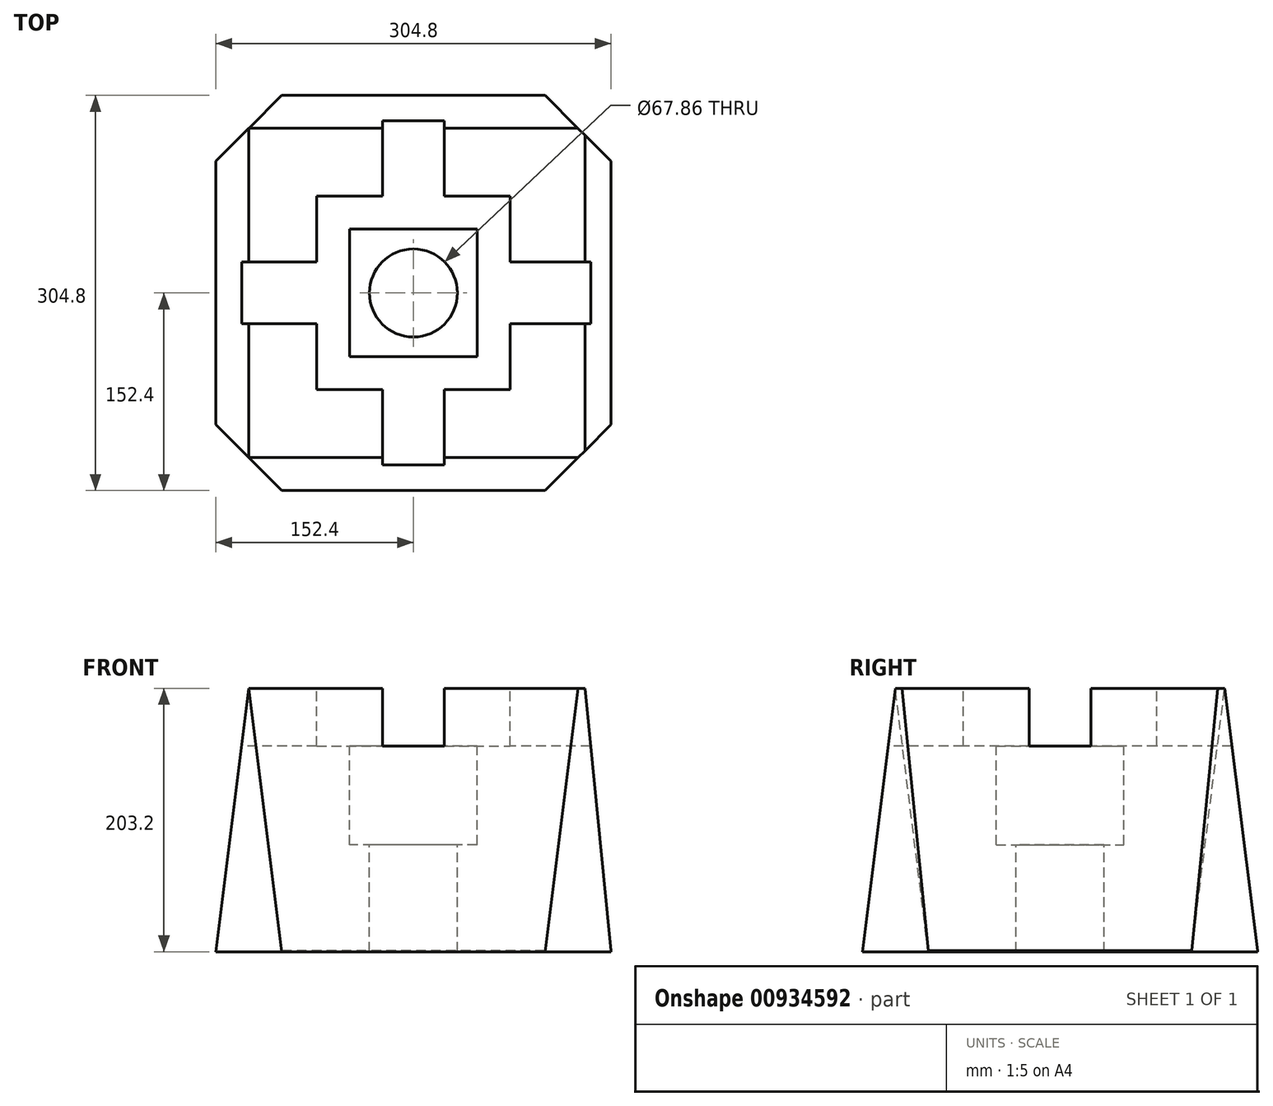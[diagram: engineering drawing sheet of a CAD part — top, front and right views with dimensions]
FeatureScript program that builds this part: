
annotation { "Feature Type Name" : "Feature", "Feature Type Description" : "" }
export const myFeature = defineFeature(function(context is Context, id is Id, definition is map)
    precondition{}
    {
        {
            var Q0;
            Q0=qCreatedBy(makeId("Top.planeOp"),FACE);
            var sketch = newSketch(context, id + "F0", { "sketchPlane" : qUnion([Q0])});
            skLineSegment(sketch, "E0.bottom", {"start": v(0, 0) * mm, "end": v(304.8, 0) * mm});
            skLineSegment(sketch, "E0.top", {"start": v(0, 304.8) * mm, "end": v(304.8, 304.8) * mm});
            skLineSegment(sketch, "E0.left", {"start": v(0, 0) * mm, "end": v(0, 304.8) * mm});
            skLineSegment(sketch, "E0.right", {"start": v(304.8, 0) * mm, "end": v(304.8, 304.8) * mm});
            skSolve(sketch);
        }
        {
            var Q0;
            Q0=makeQuery(id+"F0.imprint","IMPRINT",FACE,{"disambiguationData":[TD([[makeQuery(id+"F0.imprint","IMPRINT",EDGE,{"derivedFrom":sQuery(id+"F0.wireOp",EDGE,"E0.bottom")}),1.0]])]});
            extrude(context, id + "F1", {"entities" : qUnion([Q0]), "depth" : 203.2 * mm, "offsetDistance" : 25.4 * mm});
        }
        {
            var Q0;
            Q0=makeQuery(id+"F1.opExtrude","CAP_FACE",FACE,{"disambiguationData":[OSD([sQuery(id+"F0.wireOp",EDGE,"E0.bottom"),sQuery(id+"F0.wireOp",EDGE,"E0.top"),sQuery(id+"F0.wireOp",EDGE,"E0.left"),sQuery(id+"F0.wireOp",EDGE,"E0.right")])],"isStart":false});
            var sketch = newSketch(context, id + "F2", { "sketchPlane" : qUnion([Q0])});
            skLineSegment(sketch, "E1.bottom", {"start": v(77.79, 227.01) * mm, "end": v(227.01, 227.01) * mm});
            skLineSegment(sketch, "E1.top", {"start": v(77.79, 77.79) * mm, "end": v(227.01, 77.79) * mm});
            skLineSegment(sketch, "E1.left", {"start": v(77.79, 227.01) * mm, "end": v(77.79, 77.79) * mm});
            skLineSegment(sketch, "E1.right", {"start": v(227.01, 227.01) * mm, "end": v(227.01, 77.79) * mm});
            skSolve(sketch);
        }
        {
            var Q0;
            Q0=makeQuery(id+"F2.imprint","IMPRINT",FACE,{"disambiguationData":[TD([[makeQuery(id+"F2.imprint","IMPRINT",EDGE,{"derivedFrom":sQuery(id+"F2.wireOp",EDGE,"E1.bottom")}),-1.0]])]});
            extrude(context, id + "F3", {"entities" : qUnion([Q0]), "operationType" : NewBodyOperationType.REMOVE, "oppositeDirection" : true, "depth" : 44.45 * mm, "offsetDistance" : 25.4 * mm});
        }
        {
            var Q0;
            Q0=makeQuery(id+"F1.opExtrude","CAP_FACE",FACE,{"disambiguationData":[OSD([sQuery(id+"F0.wireOp",EDGE,"E0.bottom"),sQuery(id+"F0.wireOp",EDGE,"E0.top"),sQuery(id+"F0.wireOp",EDGE,"E0.left"),sQuery(id+"F0.wireOp",EDGE,"E0.right")])],"isStart":false});
            var sketch = newSketch(context, id + "F4", { "sketchPlane" : qUnion([Q0])});
            skLineSegment(sketch, "E2.bottom", {"start": v(128.59, 304.8) * mm, "end": v(176.21, 304.8) * mm});
            skLineSegment(sketch, "E2.top", {"start": v(128.59, 0) * mm, "end": v(176.21, 0) * mm});
            skLineSegment(sketch, "E2.left", {"start": v(128.59, 304.8) * mm, "end": v(128.59, 0) * mm});
            skLineSegment(sketch, "E2.right", {"start": v(176.21, 304.8) * mm, "end": v(176.21, 0) * mm});
            skLineSegment(sketch, "E3.bottom", {"start": v(312.2, 128.59) * mm, "end": v(-17, 128.59) * mm});
            skLineSegment(sketch, "E3.top", {"start": v(312.2, 176.21) * mm, "end": v(-17, 176.21) * mm});
            skLineSegment(sketch, "E3.left", {"start": v(312.2, 128.59) * mm, "end": v(312.2, 176.21) * mm});
            skLineSegment(sketch, "E3.right", {"start": v(-17, 128.59) * mm, "end": v(-17, 176.21) * mm});
            skSolve(sketch);
        }
        {
            var Q0;
            {var subQ0=sQuery(id+"F4.wireOp",EDGE,"E2.bottom");Q0=makeQuery(id+"F4.imprint","IMPRINT",FACE,{"disambiguationData":[TD([[makeQuery(id+"F4.imprint","IMPRINT",EDGE,{"derivedFrom":subQ0}),-1.0]])]});}
            var Q1;
            {var subQ0=sQuery(id+"F4.wireOp",EDGE,"E2.top");Q1=makeQuery(id+"F4.imprint","IMPRINT",FACE,{"disambiguationData":[TD([[makeQuery(id+"F4.imprint","IMPRINT",EDGE,{"derivedFrom":subQ0}),1.0]])]});}
            var Q2;
            {var subQ0=sQuery(id+"F4.wireOp",EDGE,"E3.bottom");var subQ1=makeQuery(id+"F1.opExtrude","CAP_EDGE",EDGE,{"disambiguationData":[OSD([sQuery(id+"F0.wireOp",EDGE,"E0.right")])],"isStart":false});var subQ2=makeQuery(id+"F4.imprint","INTERSECT",VERTEX,{"derivedFrom":[subQ1,subQ0]});Q2=makeQuery(id+"F4.imprint","IMPRINT",FACE,{"disambiguationData":[TD([[makeQuery(id+"F4.imprint","IMPRINT",EDGE,{"disambiguationData":[TD([[subQ2,-1.0]])],"derivedFrom":subQ0}),-1.0]])]});}
            var Q3;
            {var subQ0=sQuery(id+"F4.wireOp",EDGE,"E3.bottom");var subQ1=makeQuery(id+"F1.opExtrude","CAP_EDGE",EDGE,{"disambiguationData":[OSD([sQuery(id+"F0.wireOp",EDGE,"E0.left")])],"isStart":false});var subQ2=makeQuery(id+"F4.imprint","INTERSECT",VERTEX,{"derivedFrom":[subQ1,subQ0]});Q3=makeQuery(id+"F4.imprint","IMPRINT",FACE,{"disambiguationData":[TD([[makeQuery(id+"F4.imprint","IMPRINT",EDGE,{"disambiguationData":[TD([[subQ2,1.0]])],"derivedFrom":subQ0}),-1.0]])]});}
            extrude(context, id + "F5", {"entities" : qUnion([Q0, Q1, Q2, Q3]), "operationType" : NewBodyOperationType.REMOVE, "oppositeDirection" : true, "depth" : 44.45 * mm, "offsetDistance" : 25.4 * mm});
        }
        {
            var Q0;
            Q0=makeQuery(id+"F1.opExtrude","SWEPT_EDGE",EDGE,{"disambiguationData":[OSD([sQuery(id+"F0.wireOp",EDGE,"E0.bottom"),sQuery(id+"F0.wireOp",EDGE,"E0.right")])]});
            var Q1;
            Q1=makeQuery(id+"F1.opExtrude","SWEPT_EDGE",EDGE,{"disambiguationData":[OSD([sQuery(id+"F0.wireOp",EDGE,"E0.top"),sQuery(id+"F0.wireOp",EDGE,"E0.right")])]});
            var Q2;
            Q2=makeQuery(id+"F1.opExtrude","SWEPT_EDGE",EDGE,{"disambiguationData":[OSD([sQuery(id+"F0.wireOp",EDGE,"E0.bottom"),sQuery(id+"F0.wireOp",EDGE,"E0.left")])]});
            var Q3;
            Q3=makeQuery(id+"F1.opExtrude","SWEPT_EDGE",EDGE,{"disambiguationData":[OSD([sQuery(id+"F0.wireOp",EDGE,"E0.top"),sQuery(id+"F0.wireOp",EDGE,"E0.left")])]});
            chamfer(context, id + "F6", {"entities" : qUnion([Q0, Q1, Q2, Q3]), "width" : 50.8 * mm, "tangentPropagation" : true});
        }
        {
            var Q0;
            Q0=makeQuery(id+"F3.boolean.opBoolean","COPY",FACE,{"derivedFrom":makeQuery(id+"F3.opExtrude","CAP_FACE",FACE,{"disambiguationData":[OSD([sQuery(id+"F2.wireOp",EDGE,"E1.bottom"),sQuery(id+"F2.wireOp",EDGE,"E1.top"),sQuery(id+"F2.wireOp",EDGE,"E1.left"),sQuery(id+"F2.wireOp",EDGE,"E1.right")])],"isStart":false})});
            var sketch = newSketch(context, id + "F7", { "sketchPlane" : qUnion([Q0])});
            skCircle(sketch, "E4", {"center": v(152.4, 152.4) * mm, "radius": 33.93 * mm});
            skSolve(sketch);
        }
        {
            var Q0;
            Q0=makeQuery(id+"F7.imprint","IMPRINT",FACE,{"disambiguationData":[TD([[makeQuery(id+"F7.imprint","IMPRINT",EDGE,{"derivedFrom":sQuery(id+"F7.wireOp",EDGE,"E4")}),1.0]])]});
            extrude(context, id + "F8", {"entities" : qUnion([Q0]), "operationType" : NewBodyOperationType.REMOVE, "endBound" : BoundingType.THROUGH_ALL, "oppositeDirection" : true, "depth" : 25.4 * mm, "offsetDistance" : 25.4 * mm});
        }
        {
            var Q0;
            Q0=makeQuery(id+"F3.boolean.opBoolean","COPY",FACE,{"derivedFrom":makeQuery(id+"F3.opExtrude","CAP_FACE",FACE,{"disambiguationData":[OSD([sQuery(id+"F2.wireOp",EDGE,"E1.bottom"),sQuery(id+"F2.wireOp",EDGE,"E1.top"),sQuery(id+"F2.wireOp",EDGE,"E1.left"),sQuery(id+"F2.wireOp",EDGE,"E1.right")])],"isStart":false})});
            var sketch = newSketch(context, id + "F9", { "sketchPlane" : qUnion([Q0])});
            skLineSegment(sketch, "E5.bottom", {"start": v(201.61, 103.19) * mm, "end": v(103.19, 103.19) * mm});
            skLineSegment(sketch, "E5.top", {"start": v(201.61, 201.61) * mm, "end": v(103.19, 201.61) * mm});
            skLineSegment(sketch, "E5.left", {"start": v(201.61, 103.19) * mm, "end": v(201.61, 201.61) * mm});
            skLineSegment(sketch, "E5.right", {"start": v(103.19, 103.19) * mm, "end": v(103.19, 201.61) * mm});
            skPoint(sketch, "E5.middle", {"position": v(152.4, 152.4) * mm});
            skSolve(sketch);
        }
        {
            var Q0;
            {var subQ27=sQuery(id+"F9.wireOp",EDGE,"E5.left");Q0=makeQuery(id+"F9.imprint","IMPRINT",FACE,{"disambiguationData":[TD([[makeQuery(id+"F9.imprint","IMPRINT",EDGE,{"derivedFrom":subQ27}),1.0]])]});}
            extrude(context, id + "F10", {"entities" : qUnion([Q0]), "operationType" : NewBodyOperationType.REMOVE, "oppositeDirection" : true, "depth" : 76.2 * mm, "offsetDistance" : 25.4 * mm});
        }
        {
            var Q0;
            Q0=makeQuery(id+"F1.opExtrude","SWEPT_FACE",FACE,{"disambiguationData":[OSD([sQuery(id+"F0.wireOp",EDGE,"E0.bottom")])]});
            var sketch = newSketch(context, id + "F11", { "sketchPlane" : qUnion([Q0])});
            skLineSegment(sketch, "E6", {"start": v(0, 0) * mm, "end": v(25.4, 203.33) * mm});
            skLineSegment(sketch, "E7", {"start": v(0, 203.27) * mm, "end": v(25.4, 203.27) * mm});
            skLineSegment(sketch, "E8", {"start": v(0, 203.27) * mm, "end": v(0, 0) * mm});
            skLineSegment(sketch, "E9", {"start": v(304.9, 0) * mm, "end": v(304.9, 203.4) * mm});
            skLineSegment(sketch, "E10", {"start": v(304.9, 203.4) * mm, "end": v(284.65, 203.4) * mm});
            skLineSegment(sketch, "E11", {"start": v(284.65, 203.4) * mm, "end": v(304.9, 0) * mm});
            skSolve(sketch);
        }
        {
            var Q0;
            {var subQ2=sQuery(id+"F11.wireOp",EDGE,"E7");Q0=makeQuery(id+"F11.imprint","IMPRINT",FACE,{"disambiguationData":[TD([[makeQuery(id+"F11.imprint","IMPRINT",EDGE,{"derivedFrom":subQ2}),-1.0]])]});}
            var Q1;
            Q1=makeQuery(id+"F11.imprint","IMPRINT",FACE,{"disambiguationData":[TD([[makeQuery(id+"F11.imprint","IMPRINT",EDGE,{"derivedFrom":sQuery(id+"F11.wireOp",EDGE,"E9")}),1.0]])]});
            extrude(context, id + "F12", {"entities" : qUnion([Q0, Q1]), "operationType" : NewBodyOperationType.REMOVE, "endBound" : BoundingType.THROUGH_ALL, "oppositeDirection" : true, "depth" : 25.4 * mm, "offsetDistance" : 25.4 * mm});
        }
        {
            var Q0;
            Q0=makeQuery(id+"F1.opExtrude","SWEPT_FACE",FACE,{"disambiguationData":[OSD([sQuery(id+"F0.wireOp",EDGE,"E0.right")])]});
            var sketch = newSketch(context, id + "F13", { "sketchPlane" : qUnion([Q0])});
            skLineSegment(sketch, "E12", {"start": v(0, 0) * mm, "end": v(0, 203.3) * mm});
            skLineSegment(sketch, "E13", {"start": v(0, 203.3) * mm, "end": v(25.4, 203.3) * mm});
            skLineSegment(sketch, "E14", {"start": v(25.4, 203.3) * mm, "end": v(0, 0) * mm});
            skLineSegment(sketch, "E15", {"start": v(304.92, 0) * mm, "end": v(304.92, 203.66) * mm});
            skLineSegment(sketch, "E16", {"start": v(304.92, 203.66) * mm, "end": v(279.52, 203.66) * mm});
            skLineSegment(sketch, "E17", {"start": v(279.52, 203.66) * mm, "end": v(304.92, 0) * mm});
            skSolve(sketch);
        }
        {
            var Q0;
            Q0=makeQuery(id+"F13.imprint","IMPRINT",FACE,{"disambiguationData":[TD([[makeQuery(id+"F13.imprint","IMPRINT",EDGE,{"derivedFrom":sQuery(id+"F13.wireOp",EDGE,"E12")}),-1.0]])]});
            var Q1;
            Q1=makeQuery(id+"F13.imprint","IMPRINT",FACE,{"disambiguationData":[TD([[makeQuery(id+"F13.imprint","IMPRINT",EDGE,{"derivedFrom":sQuery(id+"F13.wireOp",EDGE,"E15")}),1.0]])]});
            extrude(context, id + "F14", {"entities" : qUnion([Q0, Q1]), "operationType" : NewBodyOperationType.REMOVE, "endBound" : BoundingType.THROUGH_ALL, "oppositeDirection" : true, "depth" : 25.4 * mm, "offsetDistance" : 25.4 * mm});
        }
    });
